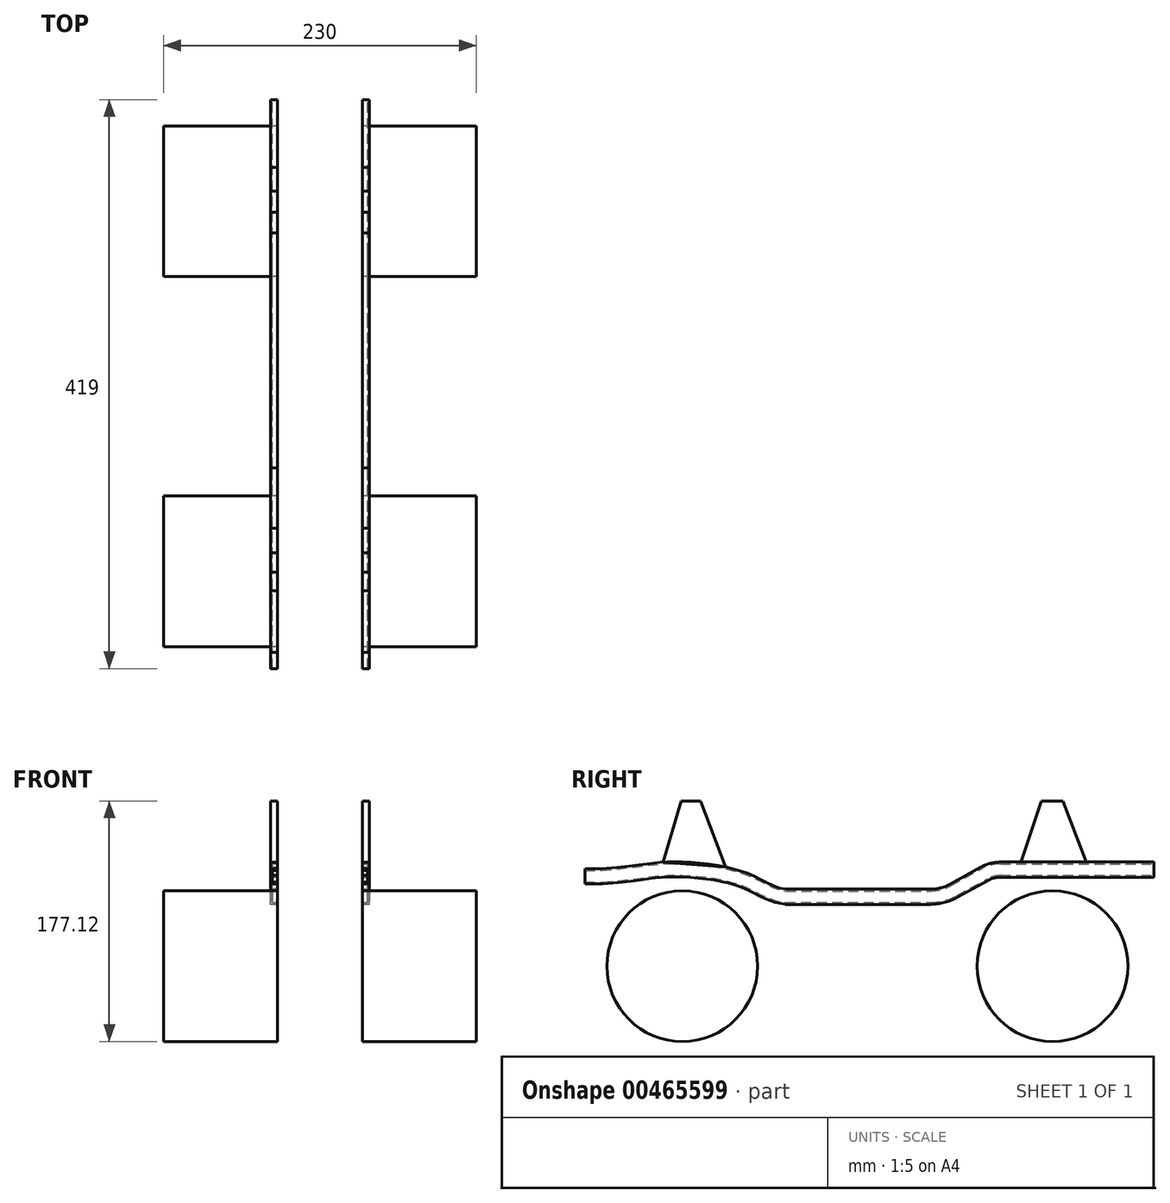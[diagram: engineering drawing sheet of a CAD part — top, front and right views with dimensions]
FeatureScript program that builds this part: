
annotation { "Feature Type Name" : "Feature", "Feature Type Description" : "" }
export const myFeature = defineFeature(function(context is Context, id is Id, definition is map)
    precondition{}
    {
        {
            var Q0;
            Q0=qCreatedBy(makeId("Front.planeOp"),FACE);
            var sketch = newSketch(context, id + "F0", { "sketchPlane" : qUnion([Q0])});
            skLineSegment(sketch, "E0.bottom", {"start": v(31.35, 0) * mm, "end": v(36.35, 0) * mm});
            skLineSegment(sketch, "E0.top", {"start": v(31.35, -11.12) * mm, "end": v(36.35, -11.12) * mm});
            skLineSegment(sketch, "E0.left", {"start": v(31.35, 0) * mm, "end": v(31.35, -1.3) * mm});
            skLineSegment(sketch, "E0.right", {"start": v(36.35, 0) * mm, "end": v(36.35, -11.12) * mm});
            skLineSegment(sketch, "E1", {"start": v(31.35, -1.3) * mm, "end": v(35.05, -1.3) * mm});
            skLineSegment(sketch, "E2", {"start": v(31.35, -11.12) * mm, "end": v(31.35, -9.82) * mm});
            skLineSegment(sketch, "E3", {"start": v(31.35, -9.82) * mm, "end": v(35.05, -9.82) * mm});
            skLineSegment(sketch, "E4", {"start": v(35.05, -9.82) * mm, "end": v(35.05, -1.3) * mm});
            skLineSegment(sketch, "E5.MirrorCS", {"start": v(-36.35, 0) * mm, "end": v(-36.35, -11.12) * mm});
            skLineSegment(sketch, "E6.MirrorCS", {"start": v(-35.05, -9.82) * mm, "end": v(-35.05, -1.3) * mm});
            skLineSegment(sketch, "E7.MirrorCS", {"start": v(-31.35, -1.3) * mm, "end": v(-35.05, -1.3) * mm});
            skLineSegment(sketch, "E8.MirrorCS", {"start": v(-31.35, 0) * mm, "end": v(-31.35, -1.3) * mm});
            skLineSegment(sketch, "E9.MirrorCS", {"start": v(-31.35, 0) * mm, "end": v(-36.35, 0) * mm});
            skLineSegment(sketch, "E10.MirrorCS", {"start": v(-31.35, -9.82) * mm, "end": v(-35.05, -9.82) * mm});
            skLineSegment(sketch, "E11.MirrorCS", {"start": v(-31.35, -11.12) * mm, "end": v(-31.35, -9.82) * mm});
            skLineSegment(sketch, "E12.MirrorCS", {"start": v(-31.35, -11.12) * mm, "end": v(-36.35, -11.12) * mm});
            skSolve(sketch);
        }
        {
            var Q0;
            Q0=qCreatedBy(makeId("Right.planeOp"),FACE);
            var sketch = newSketch(context, id + "F1", { "sketchPlane" : qUnion([Q0])});
            skLineSegment(sketch, "E13", {"start": v(0, 0) * mm, "end": v(12, 0) * mm});
            skLineSegment(sketch, "E14", {"start": v(148, -15) * mm, "end": v(254.28, -15) * mm});
            skLineSegment(sketch, "E15", {"start": v(268.76, -11.27) * mm, "end": v(291.52, 1.27) * mm});
            skLineSegment(sketch, "E16", {"start": v(306, 5) * mm, "end": v(419, 5) * mm});
            skFitSpline(sketch, "E17", {"points": [v(12, 0) * mm, v(58.99, 5) * mm, v(94.57, 3.05) * mm, v(124.83, -5.6) * mm, v(148, -15) * mm], "startDerivative": vector(295.88, 25.77) * mm, "endDerivative": vector(112.75, -9.79) * mm});
            skPoint(sketch, "E18.visualSharp", {"position": v(262, -15) * mm});
            skArc(sketch, "E18.filletArc", {"start": v(254.28, -15) * mm, "mid": v(261.76, -14.05) * mm, "end": v(268.76, -11.27) * mm});
            skPoint(sketch, "E19.visualSharp", {"position": v(298.28, 5) * mm});
            skArc(sketch, "E19.filletArc", {"start": v(306, 5) * mm, "mid": v(298.52, 4.05) * mm, "end": v(291.52, 1.27) * mm});
            skSolve(sketch);
        }
        {
            var Q0;
            Q0 = qSketchRegion(id + "F0", true);
            var Q1;
            Q1 = qConstructionFilter(qBodyType(qCreatedBy(id + "F1" ,EDGE), BodyType.WIRE), ConstructionObject.NO);
            sweep(context, id + "F2", {"profiles" : qUnion([Q0]), "path" : qUnion([Q1])});
        }
        {
            var Q0;
            Q0=makeQuery(id+"F2.opSweep","SWEPT_FACE",FACE,{"disambiguationData":[OSD([sQuery(id+"F0.wireOp",EDGE,"E0.right"),sQuery(id+"F1.wireOp",EDGE,"E13")])]});
            var sketch = newSketch(context, id + "F3", { "sketchPlane" : qUnion([Q0])});
            skLineSegment(sketch, "E20", {"start": v(57.44, 4.92) * mm, "end": v(70.91, 50) * mm});
            skLineSegment(sketch, "E21", {"start": v(70.91, 50) * mm, "end": v(85.2, 50) * mm});
            skLineSegment(sketch, "E22", {"start": v(85.2, 50) * mm, "end": v(103.44, 1.45) * mm});
            skLineSegment(sketch, "E23", {"start": v(321, 5) * mm, "end": v(336.03, 50) * mm});
            skLineSegment(sketch, "E24", {"start": v(351.7, 50) * mm, "end": v(369, 5) * mm});
            skLineSegment(sketch, "E25", {"start": v(336.03, 50) * mm, "end": v(351.7, 50) * mm});
            skLineSegment(sketch, "E26", {"start": v(57.44, 4.92) * mm, "end": v(103.44, 1.45) * mm});
            skLineSegment(sketch, "E27", {"start": v(321, 5) * mm, "end": v(369, 5) * mm});
            skSolve(sketch);
        }
        {
            var Q0;
            Q0 = qSketchRegion(id + "F3", true);
            var Q1;
            Q1=makeQuery(id+"F2.opSweep","SWEPT_FACE",FACE,{"disambiguationData":[OSD([sQuery(id+"F0.wireOp",EDGE,"E5.MirrorCS"),sQuery(id+"F1.wireOp",EDGE,"E13")])]});
            extrude(context, id + "F4", {"entities" : qUnion([Q0]), "endBound" : BoundingType.UP_TO_SURFACE, "oppositeDirection" : true, "endBoundEntityFace" : qUnion([Q1]), "depth" : 25 * mm});
        }
        {
            var Q0;
            Q0=qCreatedBy(makeId("Right.planeOp"),FACE);
            var sketch = newSketch(context, id + "F5", { "sketchPlane" : qUnion([Q0])});
            skCircle(sketch, "E28", {"center": v(71.66, -71.62) * mm, "radius": 55.5 * mm});
            skCircle(sketch, "E29", {"center": v(344.17, -71.62) * mm, "radius": 55.5 * mm});
            skSolve(sketch);
        }
        {
            var Q0;
            Q0=makeQuery(id+"F5.imprint","IMPRINT",FACE,{"disambiguationData":[TD([[makeQuery(id+"F5.imprint","IMPRINT",EDGE,{"derivedFrom":sQuery(id+"F5.wireOp",EDGE,"E28")}),1.0]])]});
            var Q1;
            Q1=makeQuery(id+"F5.imprint","IMPRINT",FACE,{"disambiguationData":[TD([[makeQuery(id+"F5.imprint","IMPRINT",EDGE,{"derivedFrom":sQuery(id+"F5.wireOp",EDGE,"E29")}),1.0]])]});
            extrude(context, id + "F6", {"entities" : qUnion([Q0, Q1]), "endBound" : BoundingType.SYMMETRIC, "depth" : 230 * mm});
        }
        {
            var Q0;
            Q0=qCreatedBy(makeId("Front.planeOp"),FACE);
            var sketch = newSketch(context, id + "F7", { "sketchPlane" : qUnion([Q0])});
            skLineSegment(sketch, "E30.bottom", {"start": v(-31.35, 64.06) * mm, "end": v(31.35, 64.06) * mm});
            skLineSegment(sketch, "E30.top", {"start": v(-31.35, -130.96) * mm, "end": v(31.35, -130.96) * mm});
            skLineSegment(sketch, "E30.left", {"start": v(-31.35, 64.06) * mm, "end": v(-31.35, -130.96) * mm});
            skLineSegment(sketch, "E30.right", {"start": v(31.35, 64.06) * mm, "end": v(31.35, -130.96) * mm});
            skSolve(sketch);
        }
        {
            var Q0;
            Q0=makeQuery(id+"F7.imprint","IMPRINT",FACE,{"disambiguationData":[TD([[makeQuery(id+"F7.imprint","IMPRINT",EDGE,{"derivedFrom":sQuery(id+"F7.wireOp",EDGE,"E30.bottom")}),-1.0]])]});
            extrude(context, id + "F8", {"entities" : qUnion([Q0]), "operationType" : NewBodyOperationType.REMOVE, "oppositeDirection" : true, "depth" : 400 * mm});
        }
    });
